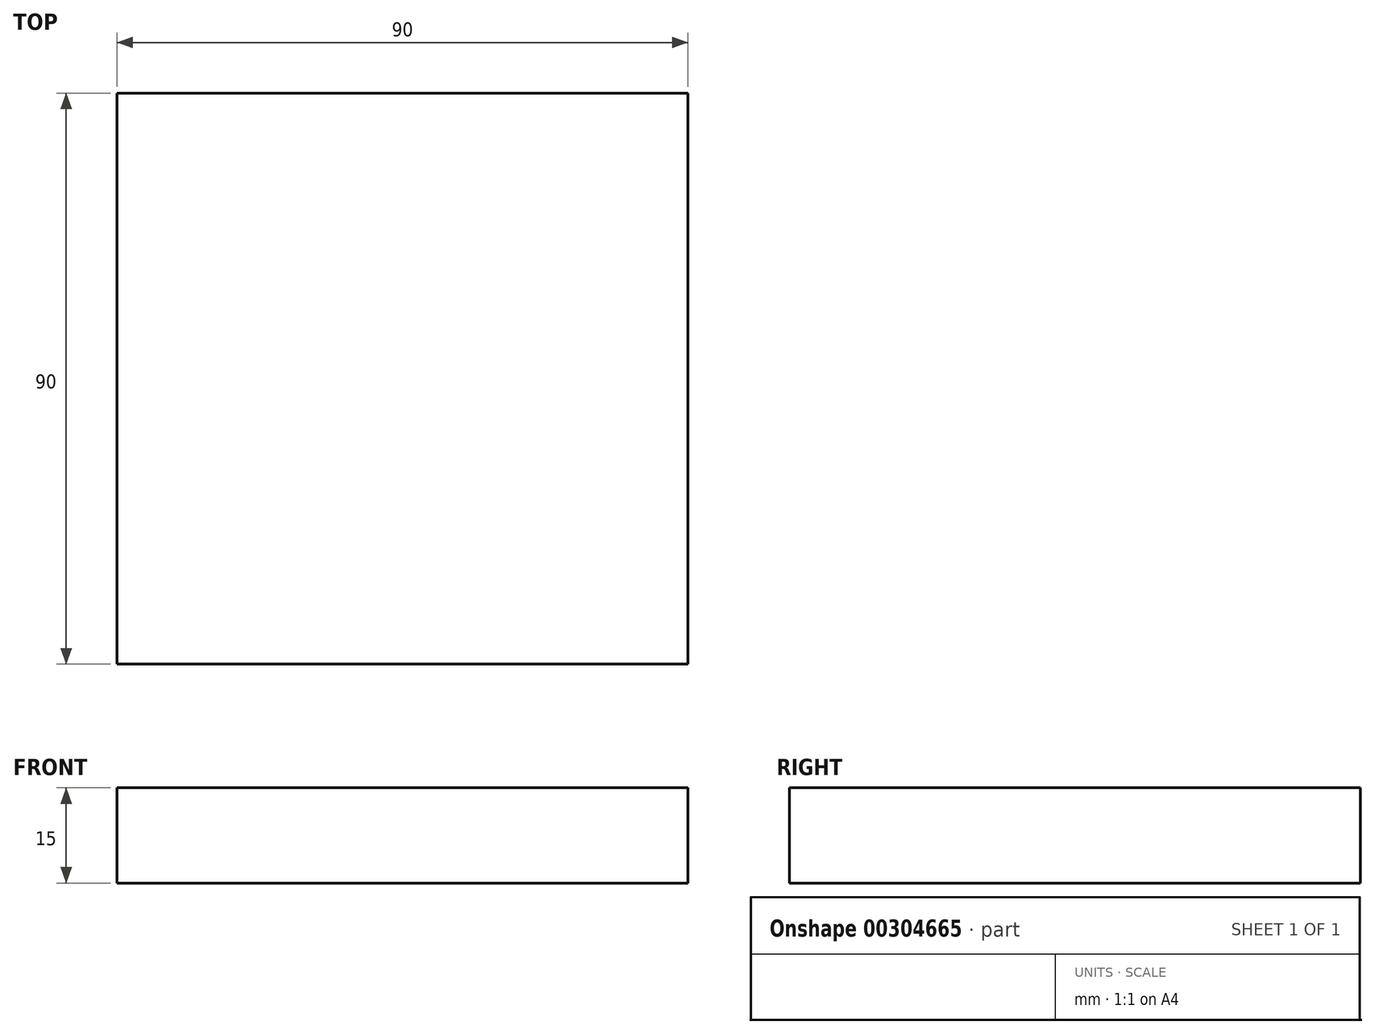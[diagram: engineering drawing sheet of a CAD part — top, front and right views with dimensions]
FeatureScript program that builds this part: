
annotation { "Feature Type Name" : "Feature", "Feature Type Description" : "" }
export const myFeature = defineFeature(function(context is Context, id is Id, definition is map)
    precondition{}
    {
        {
            var Q0;
            Q0=qCreatedBy(makeId("Top.planeOp"),FACE);
            var sketch = newSketch(context, id + "F0", { "sketchPlane" : qUnion([Q0])});
            skLineSegment(sketch, "E0.bottom", {"start": v(45, 45) * mm, "end": v(-45, 45) * mm});
            skLineSegment(sketch, "E0.top", {"start": v(45, -45) * mm, "end": v(-45, -45) * mm});
            skLineSegment(sketch, "E0.left", {"start": v(45, 45) * mm, "end": v(45, -45) * mm});
            skLineSegment(sketch, "E0.right", {"start": v(-45, 45) * mm, "end": v(-45, -45) * mm});
            skPoint(sketch, "E0.middle", {"position": v(0, 0) * mm});
            skSolve(sketch);
        }
        {
            var Q0;
            Q0=qSketchRegion(id+"F0",true);
            extrude(context, id + "F1", {"entities" : qUnion([Q0]), "depth" : 15 * mm});
        }
    });
